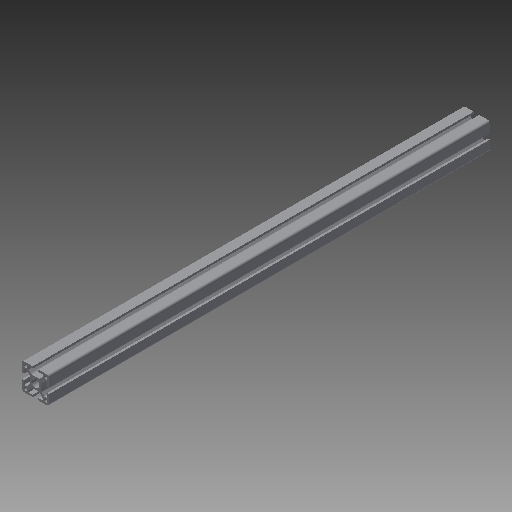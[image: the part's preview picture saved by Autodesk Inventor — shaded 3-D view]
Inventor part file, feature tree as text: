
AUTODESK INVENTOR PART (.ipt)
format: ipt  version: 2018 (Build 220112000, 112)  size: 222,720 bytes
history: native  units: mm
features: other x42, sketch x5, hole x4, extrude x1
ambient origin geometry x8: Origin, YZ Plane, XZ Plane, XY Plane, X Axis, Y Axis, Z Axis, Center Point
bodies: Solid1 (feature_tree)
feature tree (52):
  extrude  "Extrusion1"  [1 undecoded]
  hole  "Drilling 1"  [1 undecoded]
  hole  "Drilling 2"  [1 undecoded]
  hole  "Drilling 3"  [1 undecoded]
  hole  "Drilling 4"  [1 undecoded]
  other  "side_4d_XY"
  other  "side_4d_YZ"
  other  "side_4d_ZX"
  other  "side_4d_X"
  other  "side_4d_Y"
  other  "side_4d_Z"
  other  "side_4d_Center"
  other  "side_1a_XY"
  other  "side_1a_YZ"
  other  "side_1a_ZX"
  other  "side_1a_X"
  other  "side_1a_Y"
  other  "side_1a_Z"
  other  "side_1a_Center"
  other  "side_2b_XY"
  other  "side_2b_YZ"
  other  "side_2b_ZX"
  other  "side_2b_X"
  other  "side_2b_Y"
  other  "side_2b_Z"
  other  "side_2b_Center"
  other  "side_3c_XY"
  other  "side_3c_YZ"
  other  "side_3c_ZX"
  other  "side_3c_X"
  other  "side_3c_Y"
  other  "side_3c_Z"
  other  "side_3c_Center"
  other  "end_XY"
  other  "end_YZ"
  other  "end_ZX"
  other  "end_X"
  other  "end_Y"
  other  "end_Z"
  other  "end_Center"
  other  "start_XY"
  other  "start_YZ"
  other  "start_ZX"
  other  "start_X"
  other  "start_Y"
  other  "start_Z"
  other  "start_Center"
  sketch  "Skizze_1"  dims[d0=660.0mm d1=0.0mm]
  sketch  "Sketch2"  dims[d2=5.0mm d3=6.0mm d4=4.0mm d5=2.0mm d6=90.0deg d7=6000.0mm d8=0.0mm]
  sketch  "Sketch3"  dims[d9=5.0mm d10=6.0mm d11=4.0mm d12=2.0mm d13=90.0deg d14=6000.0mm d15=0.0mm]
  sketch  "Sketch4"  dims[d16=5.0mm d17=6.0mm d18=4.0mm d19=2.0mm d20=90.0deg d21=6000.0mm d22=0.0mm]
  sketch  "Sketch5"  dims[d23=5.0mm d24=6.0mm d25=4.0mm d26=2.0mm d27=90.0deg d28=6000.0mm d29=0.0mm]
note: 5 required parameter values undecoded (feature->parameter linkage not recoverable at this tier; creation-order binding heuristic only, values carry confidence <= 0.55)
